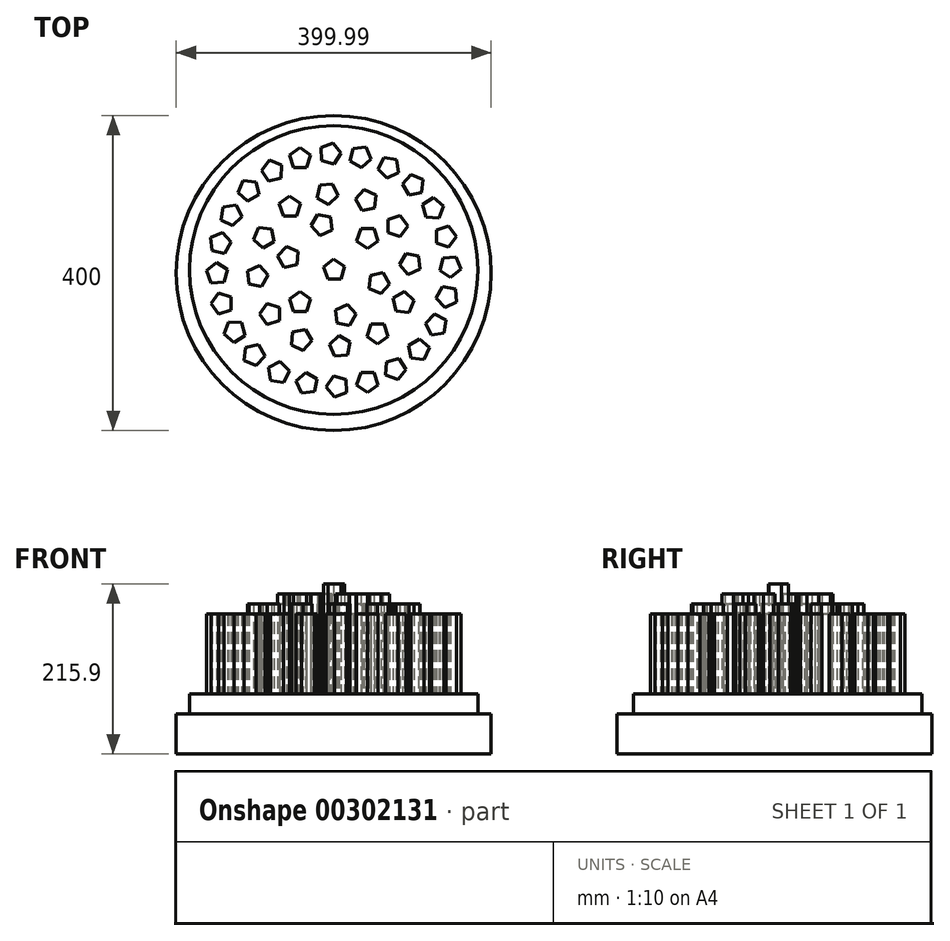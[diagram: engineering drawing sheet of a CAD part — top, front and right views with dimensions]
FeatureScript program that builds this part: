
annotation { "Feature Type Name" : "Feature", "Feature Type Description" : "" }
export const myFeature = defineFeature(function(context is Context, id is Id, definition is map)
    precondition{}
    {
        {
            var Q0;
            Q0=qCreatedBy(makeId("Top.planeOp"),FACE);
            var sketch = newSketch(context, id + "F0", { "sketchPlane" : qUnion([Q0])});
            skCircle(sketch, "E0.cCircle", {"center": v(0, 0) * mm, "radius": 11.36 * mm, "construction": true});
            skLineSegment(sketch, "E0.0", {"start": v(8.25, -11.36) * mm, "end": v(-8.25, -11.36) * mm});
            skLineSegment(sketch, "E0.1", {"start": v(-8.25, -11.36) * mm, "end": v(-13.35, 4.34) * mm});
            skLineSegment(sketch, "E0.2", {"start": v(-13.35, 4.34) * mm, "end": v(0, 14.04) * mm});
            skLineSegment(sketch, "E0.3", {"start": v(0, 14.04) * mm, "end": v(13.35, 4.34) * mm});
            skLineSegment(sketch, "E0.4", {"start": v(13.35, 4.34) * mm, "end": v(8.25, -11.36) * mm});
            skPoint(sketch, "E0.0.midPoint", {"position": v(0, -11.36) * mm});
            skLineSegment(sketch, "E1.1.0", {"start": v(46.76, -25.65) * mm, "end": v(45.03, -9.23) * mm});
            skLineSegment(sketch, "E1.1.1", {"start": v(45.03, -9.23) * mm, "end": v(60.11, -2.52) * mm});
            skLineSegment(sketch, "E1.1.2", {"start": v(60.11, -2.52) * mm, "end": v(71.16, -14.79) * mm});
            skLineSegment(sketch, "E1.1.3", {"start": v(71.16, -14.79) * mm, "end": v(62.9, -29.08) * mm});
            skLineSegment(sketch, "E1.1.4", {"start": v(62.9, -29.08) * mm, "end": v(46.76, -25.65) * mm});
            skLineSegment(sketch, "E1.2.0", {"start": v(102.78, 11.41) * mm, "end": v(87.7, 18.13) * mm});
            skLineSegment(sketch, "E1.2.1", {"start": v(87.7, 18.13) * mm, "end": v(89.43, 34.54) * mm});
            skLineSegment(sketch, "E1.2.2", {"start": v(89.43, 34.54) * mm, "end": v(105.57, 37.97) * mm});
            skLineSegment(sketch, "E1.2.3", {"start": v(105.57, 37.97) * mm, "end": v(113.83, 23.68) * mm});
            skLineSegment(sketch, "E1.2.4", {"start": v(113.83, 23.68) * mm, "end": v(102.78, 11.41) * mm});
            skLineSegment(sketch, "E1.3.0", {"start": v(98.7, 78.47) * mm, "end": v(85.34, 68.76) * mm});
            skLineSegment(sketch, "E1.3.1", {"start": v(85.34, 68.76) * mm, "end": v(72, 78.47) * mm});
            skLineSegment(sketch, "E1.3.2", {"start": v(72, 78.47) * mm, "end": v(77.1, 94.16) * mm});
            skLineSegment(sketch, "E1.3.3", {"start": v(77.1, 94.16) * mm, "end": v(93.6, 94.16) * mm});
            skLineSegment(sketch, "E1.3.4", {"start": v(93.6, 94.16) * mm, "end": v(98.7, 78.47) * mm});
            skLineSegment(sketch, "E1.4.2", {"start": v(25.23, 85.32) * mm, "end": v(14.19, 97.6) * mm});
            skLineSegment(sketch, "E1.5.0", {"start": v(42.73, 55.32) * mm, "end": v(56.41, 46.1) * mm});
            skLineSegment(sketch, "E1.5.1", {"start": v(56.41, 46.1) * mm, "end": v(51.86, 30.22) * mm});
            skLineSegment(sketch, "E1.5.2", {"start": v(51.86, 30.22) * mm, "end": v(35.37, 29.65) * mm});
            skLineSegment(sketch, "E1.5.3", {"start": v(35.37, 29.65) * mm, "end": v(29.72, 45.16) * mm});
            skLineSegment(sketch, "E1.5.4", {"start": v(29.72, 45.16) * mm, "end": v(42.73, 55.32) * mm});
            skPoint(sketch, "E1.center", {"position": v(42.67, 41.4) * mm});
            skLineSegment(sketch, "E2.1.0", {"start": v(-17.44, 71.39) * mm, "end": v(-2.36, 64.68) * mm});
            skLineSegment(sketch, "E2.1.1", {"start": v(-2.36, 64.68) * mm, "end": v(-4.08, 48.26) * mm});
            skLineSegment(sketch, "E2.1.2", {"start": v(-4.08, 48.26) * mm, "end": v(-20.23, 44.83) * mm});
            skLineSegment(sketch, "E2.1.3", {"start": v(-20.23, 44.83) * mm, "end": v(-28.48, 59.12) * mm});
            skLineSegment(sketch, "E2.1.4", {"start": v(-28.48, 59.12) * mm, "end": v(-17.44, 71.39) * mm});
            skLineSegment(sketch, "E2.2.0", {"start": v(38.59, 108.45) * mm, "end": v(40.31, 92.04) * mm});
            skLineSegment(sketch, "E2.2.1", {"start": v(40.31, 92.04) * mm, "end": v(25.23, 85.32) * mm});
            skLineSegment(sketch, "E2.2.3", {"start": v(14.19, 97.6) * mm, "end": v(22.44, 111.88) * mm});
            skLineSegment(sketch, "E2.2.4", {"start": v(22.44, 111.88) * mm, "end": v(38.59, 108.45) * mm});
            skLineSegment(sketch, "E2.anchor1", {"start": v(42.67, 41.4) * mm, "end": v(-8.25, -11.36) * mm, "construction": true});
            skLineSegment(sketch, "E3.0", {"start": v(-4.82, 110.21) * mm, "end": v(-21.32, 110.21) * mm});
            skLineSegment(sketch, "E3.1", {"start": v(-21.32, 110.21) * mm, "end": v(-26.42, 125.91) * mm});
            skLineSegment(sketch, "E3.2", {"start": v(-26.42, 125.91) * mm, "end": v(-13.07, 135.61) * mm});
            skLineSegment(sketch, "E3.3", {"start": v(-13.07, 135.61) * mm, "end": v(0.28, 125.91) * mm});
            skLineSegment(sketch, "E3.4", {"start": v(0.28, 125.91) * mm, "end": v(-4.82, 110.21) * mm});
            skPoint(sketch, "E3.0.midPoint", {"position": v(-13.07, 110.21) * mm});
            skLineSegment(sketch, "E4.1.0", {"start": v(41.5, 150.86) * mm, "end": v(48.22, 135.78) * mm});
            skLineSegment(sketch, "E4.1.1", {"start": v(25.09, 149.14) * mm, "end": v(41.5, 150.86) * mm});
            skLineSegment(sketch, "E4.1.2", {"start": v(21.66, 133) * mm, "end": v(25.09, 149.14) * mm});
            skLineSegment(sketch, "E4.1.3", {"start": v(35.95, 124.74) * mm, "end": v(21.66, 133) * mm});
            skLineSegment(sketch, "E4.1.4", {"start": v(48.22, 135.78) * mm, "end": v(35.95, 124.74) * mm});
            skLineSegment(sketch, "E4.2.0", {"start": v(96.4, 136.78) * mm, "end": v(94.66, 120.37) * mm});
            skLineSegment(sketch, "E4.2.1", {"start": v(81.31, 143.5) * mm, "end": v(96.4, 136.78) * mm});
            skLineSegment(sketch, "E4.2.2", {"start": v(70.27, 131.23) * mm, "end": v(81.31, 143.5) * mm});
            skLineSegment(sketch, "E4.2.3", {"start": v(78.52, 116.93) * mm, "end": v(70.27, 131.23) * mm});
            skLineSegment(sketch, "E4.2.4", {"start": v(94.66, 120.37) * mm, "end": v(78.52, 116.93) * mm});
            skLineSegment(sketch, "E4.3.0", {"start": v(136.88, 97.14) * mm, "end": v(127.18, 83.79) * mm});
            skLineSegment(sketch, "E4.3.1", {"start": v(127.18, 110.5) * mm, "end": v(136.88, 97.14) * mm});
            skLineSegment(sketch, "E4.3.2", {"start": v(111.48, 105.4) * mm, "end": v(127.18, 110.5) * mm});
            skLineSegment(sketch, "E4.3.3", {"start": v(111.48, 88.9) * mm, "end": v(111.48, 105.4) * mm});
            skLineSegment(sketch, "E4.3.4", {"start": v(127.18, 83.79) * mm, "end": v(111.48, 88.9) * mm});
            skLineSegment(sketch, "E4.4.0", {"start": v(152.13, 42.57) * mm, "end": v(137.05, 35.86) * mm});
            skLineSegment(sketch, "E4.4.1", {"start": v(150.4, 58.99) * mm, "end": v(152.13, 42.57) * mm});
            skLineSegment(sketch, "E4.4.2", {"start": v(134.26, 62.42) * mm, "end": v(150.4, 58.99) * mm});
            skLineSegment(sketch, "E4.4.3", {"start": v(126, 48.12) * mm, "end": v(134.26, 62.42) * mm});
            skLineSegment(sketch, "E4.4.4", {"start": v(137.05, 35.86) * mm, "end": v(126, 48.12) * mm});
            skLineSegment(sketch, "E4.5.0", {"start": v(138.05, -12.32) * mm, "end": v(121.64, -10.6) * mm});
            skLineSegment(sketch, "E4.5.1", {"start": v(144.76, 2.76) * mm, "end": v(138.05, -12.32) * mm});
            skLineSegment(sketch, "E4.5.2", {"start": v(132.5, 13.8) * mm, "end": v(144.76, 2.76) * mm});
            skLineSegment(sketch, "E4.5.3", {"start": v(118.2, 5.55) * mm, "end": v(132.5, 13.8) * mm});
            skLineSegment(sketch, "E4.5.4", {"start": v(121.64, -10.6) * mm, "end": v(118.2, 5.55) * mm});
            skLineSegment(sketch, "E4.6.0", {"start": v(98.41, -52.8) * mm, "end": v(85.06, -43.1) * mm});
            skLineSegment(sketch, "E4.6.1", {"start": v(111.77, -43.1) * mm, "end": v(98.41, -52.8) * mm});
            skLineSegment(sketch, "E4.6.2", {"start": v(106.67, -27.4) * mm, "end": v(111.77, -43.1) * mm});
            skLineSegment(sketch, "E4.6.3", {"start": v(90.16, -27.4) * mm, "end": v(106.67, -27.4) * mm});
            skLineSegment(sketch, "E4.6.4", {"start": v(85.06, -43.1) * mm, "end": v(90.16, -27.4) * mm});
            skLineSegment(sketch, "E4.7.0", {"start": v(43.84, -68.06) * mm, "end": v(37.13, -52.98) * mm});
            skLineSegment(sketch, "E4.7.1", {"start": v(60.26, -66.33) * mm, "end": v(43.84, -68.06) * mm});
            skLineSegment(sketch, "E4.7.2", {"start": v(63.69, -50.19) * mm, "end": v(60.26, -66.33) * mm});
            skLineSegment(sketch, "E4.7.3", {"start": v(49.4, -41.93) * mm, "end": v(63.69, -50.19) * mm});
            skLineSegment(sketch, "E4.7.4", {"start": v(37.13, -52.98) * mm, "end": v(49.4, -41.93) * mm});
            skLineSegment(sketch, "E4.8.0", {"start": v(-11.05, -53.98) * mm, "end": v(-9.32, -37.56) * mm});
            skLineSegment(sketch, "E4.8.1", {"start": v(4.03, -60.7) * mm, "end": v(-11.05, -53.98) * mm});
            skLineSegment(sketch, "E4.8.2", {"start": v(15.08, -48.42) * mm, "end": v(4.03, -60.7) * mm});
            skLineSegment(sketch, "E4.8.3", {"start": v(6.82, -34.13) * mm, "end": v(15.08, -48.42) * mm});
            skLineSegment(sketch, "E4.8.4", {"start": v(-9.32, -37.56) * mm, "end": v(6.82, -34.13) * mm});
            skLineSegment(sketch, "E4.9.0", {"start": v(-51.54, -14.34) * mm, "end": v(-41.84, -0.99) * mm});
            skLineSegment(sketch, "E4.9.1", {"start": v(-41.84, -27.7) * mm, "end": v(-51.54, -14.34) * mm});
            skLineSegment(sketch, "E4.9.2", {"start": v(-26.14, -22.6) * mm, "end": v(-41.84, -27.7) * mm});
            skLineSegment(sketch, "E4.9.3", {"start": v(-26.14, -6.09) * mm, "end": v(-26.14, -22.6) * mm});
            skLineSegment(sketch, "E4.9.4", {"start": v(-41.84, -0.99) * mm, "end": v(-26.14, -6.09) * mm});
            skLineSegment(sketch, "E4.10.0", {"start": v(-66.79, 40.23) * mm, "end": v(-51.7, 46.95) * mm});
            skLineSegment(sketch, "E4.10.1", {"start": v(-65.06, 23.82) * mm, "end": v(-66.79, 40.23) * mm});
            skLineSegment(sketch, "E4.10.2", {"start": v(-48.92, 20.39) * mm, "end": v(-65.06, 23.82) * mm});
            skLineSegment(sketch, "E4.10.3", {"start": v(-40.66, 34.68) * mm, "end": v(-48.92, 20.39) * mm});
            skLineSegment(sketch, "E4.10.4", {"start": v(-51.7, 46.95) * mm, "end": v(-40.66, 34.68) * mm});
            skLineSegment(sketch, "E4.11.0", {"start": v(-52.7, 95.12) * mm, "end": v(-36.3, 93.4) * mm});
            skLineSegment(sketch, "E4.11.1", {"start": v(-59.42, 80.04) * mm, "end": v(-52.7, 95.12) * mm});
            skLineSegment(sketch, "E4.11.2", {"start": v(-47.15, 69) * mm, "end": v(-59.42, 80.04) * mm});
            skLineSegment(sketch, "E4.11.3", {"start": v(-32.86, 77.25) * mm, "end": v(-47.15, 69) * mm});
            skLineSegment(sketch, "E4.11.4", {"start": v(-36.3, 93.4) * mm, "end": v(-32.86, 77.25) * mm});
            skLineSegment(sketch, "E5.0", {"start": v(8.25, 171.75) * mm, "end": v(-8.25, 171.75) * mm});
            skLineSegment(sketch, "E5.1", {"start": v(-8.25, 171.75) * mm, "end": v(-13.35, 187.44) * mm});
            skLineSegment(sketch, "E5.2", {"start": v(-13.35, 187.44) * mm, "end": v(0, 197.15) * mm});
            skLineSegment(sketch, "E5.3", {"start": v(0, 197.15) * mm, "end": v(13.35, 187.44) * mm});
            skLineSegment(sketch, "E5.4", {"start": v(13.35, 187.44) * mm, "end": v(8.25, 171.75) * mm});
            skLineSegment(sketch, "E6.1.0", {"start": v(-38.86, 180.8) * mm, "end": v(-23.45, 174.88) * mm});
            skLineSegment(sketch, "E6.1.1", {"start": v(-23.45, 174.88) * mm, "end": v(-24.3, 158.4) * mm});
            skLineSegment(sketch, "E6.1.2", {"start": v(-24.3, 158.4) * mm, "end": v(-40.25, 154.12) * mm});
            skLineSegment(sketch, "E6.1.3", {"start": v(-40.25, 154.12) * mm, "end": v(-49.24, 167.97) * mm});
            skLineSegment(sketch, "E6.1.4", {"start": v(-49.24, 167.97) * mm, "end": v(-38.86, 180.8) * mm});
            skLineSegment(sketch, "E6.2.0", {"start": v(-72.16, 154.94) * mm, "end": v(-55.74, 153.22) * mm});
            skLineSegment(sketch, "E6.2.1", {"start": v(-55.74, 153.22) * mm, "end": v(-52.3, 137.07) * mm});
            skLineSegment(sketch, "E6.2.2", {"start": v(-52.3, 137.07) * mm, "end": v(-66.6, 128.82) * mm});
            skLineSegment(sketch, "E6.2.3", {"start": v(-66.6, 128.82) * mm, "end": v(-78.87, 139.87) * mm});
            skLineSegment(sketch, "E6.2.4", {"start": v(-78.87, 139.87) * mm, "end": v(-72.16, 154.94) * mm});
            skLineSegment(sketch, "E6.3.0", {"start": v(-97.63, 121.36) * mm, "end": v(-81.33, 123.94) * mm});
            skLineSegment(sketch, "E6.3.1", {"start": v(-81.33, 123.94) * mm, "end": v(-73.83, 109.23) * mm});
            skLineSegment(sketch, "E6.3.2", {"start": v(-73.83, 109.23) * mm, "end": v(-85.5, 97.56) * mm});
            skLineSegment(sketch, "E6.3.3", {"start": v(-85.5, 97.56) * mm, "end": v(-100.21, 105.05) * mm});
            skLineSegment(sketch, "E6.3.4", {"start": v(-100.21, 105.05) * mm, "end": v(-97.63, 121.36) * mm});
            skLineSegment(sketch, "E6.4.0", {"start": v(-113.54, 82.32) * mm, "end": v(-98.46, 89.03) * mm});
            skLineSegment(sketch, "E6.4.1", {"start": v(-98.46, 89.03) * mm, "end": v(-87.42, 76.77) * mm});
            skLineSegment(sketch, "E6.4.2", {"start": v(-87.42, 76.77) * mm, "end": v(-95.67, 62.47) * mm});
            skLineSegment(sketch, "E6.4.3", {"start": v(-95.67, 62.47) * mm, "end": v(-111.82, 65.9) * mm});
            skLineSegment(sketch, "E6.4.4", {"start": v(-111.82, 65.9) * mm, "end": v(-113.54, 82.32) * mm});
            skLineSegment(sketch, "E6.5.0", {"start": v(-118.8, 40.5) * mm, "end": v(-105.98, 50.88) * mm});
            skLineSegment(sketch, "E6.5.1", {"start": v(-105.98, 50.88) * mm, "end": v(-92.14, 41.9) * mm});
            skLineSegment(sketch, "E6.5.2", {"start": v(-92.14, 41.9) * mm, "end": v(-96.41, 25.95) * mm});
            skLineSegment(sketch, "E6.5.3", {"start": v(-96.41, 25.95) * mm, "end": v(-112.9, 25.08) * mm});
            skLineSegment(sketch, "E6.5.4", {"start": v(-112.9, 25.08) * mm, "end": v(-118.8, 40.5) * mm});
            skLineSegment(sketch, "E6.6.0", {"start": v(-113.07, -1.27) * mm, "end": v(-103.37, 12.08) * mm});
            skLineSegment(sketch, "E6.6.1", {"start": v(-103.37, 12.08) * mm, "end": v(-87.67, 6.98) * mm});
            skLineSegment(sketch, "E6.6.2", {"start": v(-87.67, 6.98) * mm, "end": v(-87.67, -9.52) * mm});
            skLineSegment(sketch, "E6.6.3", {"start": v(-87.67, -9.52) * mm, "end": v(-103.37, -14.62) * mm});
            skLineSegment(sketch, "E6.6.4", {"start": v(-103.37, -14.62) * mm, "end": v(-113.07, -1.27) * mm});
            skLineSegment(sketch, "E6.7.0", {"start": v(-96.72, -40.13) * mm, "end": v(-90.8, -24.72) * mm});
            skLineSegment(sketch, "E6.7.1", {"start": v(-90.8, -24.72) * mm, "end": v(-74.32, -25.58) * mm});
            skLineSegment(sketch, "E6.7.2", {"start": v(-74.32, -25.58) * mm, "end": v(-70.05, -41.52) * mm});
            skLineSegment(sketch, "E6.7.3", {"start": v(-70.05, -41.52) * mm, "end": v(-83.9, -50.51) * mm});
            skLineSegment(sketch, "E6.7.4", {"start": v(-83.9, -50.51) * mm, "end": v(-96.72, -40.13) * mm});
            skLineSegment(sketch, "E6.8.0", {"start": v(-70.87, -73.43) * mm, "end": v(-69.15, -57) * mm});
            skLineSegment(sketch, "E6.8.1", {"start": v(-69.15, -57) * mm, "end": v(-53, -53.58) * mm});
            skLineSegment(sketch, "E6.8.2", {"start": v(-53, -53.58) * mm, "end": v(-44.75, -67.87) * mm});
            skLineSegment(sketch, "E6.8.3", {"start": v(-44.75, -67.87) * mm, "end": v(-55.8, -80.14) * mm});
            skLineSegment(sketch, "E6.8.4", {"start": v(-55.8, -80.14) * mm, "end": v(-70.87, -73.43) * mm});
            skLineSegment(sketch, "E6.9.0", {"start": v(-37.28, -98.9) * mm, "end": v(-39.86, -82.6) * mm});
            skLineSegment(sketch, "E6.9.1", {"start": v(-39.86, -82.6) * mm, "end": v(-25.16, -75.1) * mm});
            skLineSegment(sketch, "E6.9.2", {"start": v(-25.16, -75.1) * mm, "end": v(-13.49, -86.77) * mm});
            skLineSegment(sketch, "E6.9.3", {"start": v(-13.49, -86.77) * mm, "end": v(-20.98, -101.48) * mm});
            skLineSegment(sketch, "E6.9.4", {"start": v(-20.98, -101.48) * mm, "end": v(-37.28, -98.9) * mm});
            skLineSegment(sketch, "E6.10.0", {"start": v(1.75, -114.81) * mm, "end": v(-4.96, -99.73) * mm});
            skLineSegment(sketch, "E6.10.1", {"start": v(-4.96, -99.73) * mm, "end": v(7.3, -88.69) * mm});
            skLineSegment(sketch, "E6.10.2", {"start": v(7.3, -88.69) * mm, "end": v(21.6, -96.94) * mm});
            skLineSegment(sketch, "E6.10.3", {"start": v(21.6, -96.94) * mm, "end": v(18.17, -113.09) * mm});
            skLineSegment(sketch, "E6.10.4", {"start": v(18.17, -113.09) * mm, "end": v(1.75, -114.81) * mm});
            skLineSegment(sketch, "E6.11.0", {"start": v(43.58, -120.08) * mm, "end": v(33.2, -107.25) * mm});
            skLineSegment(sketch, "E6.11.1", {"start": v(33.2, -107.25) * mm, "end": v(42.18, -93.4) * mm});
            skLineSegment(sketch, "E6.11.2", {"start": v(42.18, -93.4) * mm, "end": v(58.13, -97.68) * mm});
            skLineSegment(sketch, "E6.11.3", {"start": v(58.13, -97.68) * mm, "end": v(58.99, -114.16) * mm});
            skLineSegment(sketch, "E6.11.4", {"start": v(58.99, -114.16) * mm, "end": v(43.58, -120.08) * mm});
            skLineSegment(sketch, "E6.12.0", {"start": v(85.34, -114.34) * mm, "end": v(72, -104.64) * mm});
            skLineSegment(sketch, "E6.12.1", {"start": v(72, -104.64) * mm, "end": v(77.1, -88.94) * mm});
            skLineSegment(sketch, "E6.12.2", {"start": v(77.1, -88.94) * mm, "end": v(93.6, -88.94) * mm});
            skLineSegment(sketch, "E6.12.3", {"start": v(93.6, -88.94) * mm, "end": v(98.7, -104.64) * mm});
            skLineSegment(sketch, "E6.12.4", {"start": v(98.7, -104.64) * mm, "end": v(85.34, -114.34) * mm});
            skLineSegment(sketch, "E6.13.0", {"start": v(124.2, -98) * mm, "end": v(108.8, -92.08) * mm});
            skLineSegment(sketch, "E6.13.1", {"start": v(108.8, -92.08) * mm, "end": v(109.65, -75.6) * mm});
            skLineSegment(sketch, "E6.13.2", {"start": v(109.65, -75.6) * mm, "end": v(125.6, -71.32) * mm});
            skLineSegment(sketch, "E6.13.3", {"start": v(125.6, -71.32) * mm, "end": v(134.59, -85.16) * mm});
            skLineSegment(sketch, "E6.13.4", {"start": v(134.59, -85.16) * mm, "end": v(124.2, -98) * mm});
            skLineSegment(sketch, "E6.14.0", {"start": v(157.5, -72.14) * mm, "end": v(141.08, -70.42) * mm});
            skLineSegment(sketch, "E6.14.1", {"start": v(141.08, -70.42) * mm, "end": v(137.65, -54.27) * mm});
            skLineSegment(sketch, "E6.14.2", {"start": v(137.65, -54.27) * mm, "end": v(151.95, -46.02) * mm});
            skLineSegment(sketch, "E6.14.3", {"start": v(151.95, -46.02) * mm, "end": v(164.21, -57.06) * mm});
            skLineSegment(sketch, "E6.14.4", {"start": v(164.21, -57.06) * mm, "end": v(157.5, -72.14) * mm});
            skLineSegment(sketch, "E6.15.0", {"start": v(182.97, -38.55) * mm, "end": v(166.67, -41.13) * mm});
            skLineSegment(sketch, "E6.15.1", {"start": v(166.67, -41.13) * mm, "end": v(159.18, -26.43) * mm});
            skLineSegment(sketch, "E6.15.2", {"start": v(159.18, -26.43) * mm, "end": v(170.85, -14.76) * mm});
            skLineSegment(sketch, "E6.15.3", {"start": v(170.85, -14.76) * mm, "end": v(185.56, -22.25) * mm});
            skLineSegment(sketch, "E6.15.4", {"start": v(185.56, -22.25) * mm, "end": v(182.97, -38.55) * mm});
            skLineSegment(sketch, "E6.16.0", {"start": v(198.89, 0.48) * mm, "end": v(183.8, -6.23) * mm});
            skLineSegment(sketch, "E6.16.1", {"start": v(183.8, -6.23) * mm, "end": v(172.76, 6.04) * mm});
            skLineSegment(sketch, "E6.16.2", {"start": v(172.76, 6.04) * mm, "end": v(181.02, 20.33) * mm});
            skLineSegment(sketch, "E6.16.3", {"start": v(181.02, 20.33) * mm, "end": v(197.16, 16.9) * mm});
            skLineSegment(sketch, "E6.16.4", {"start": v(197.16, 16.9) * mm, "end": v(198.89, 0.48) * mm});
            skLineSegment(sketch, "E6.17.0", {"start": v(204.15, 42.31) * mm, "end": v(191.33, 31.92) * mm});
            skLineSegment(sketch, "E6.17.1", {"start": v(191.33, 31.92) * mm, "end": v(177.48, 40.91) * mm});
            skLineSegment(sketch, "E6.17.2", {"start": v(177.48, 40.91) * mm, "end": v(181.76, 56.86) * mm});
            skLineSegment(sketch, "E6.17.3", {"start": v(181.76, 56.86) * mm, "end": v(198.24, 57.72) * mm});
            skLineSegment(sketch, "E6.17.4", {"start": v(198.24, 57.72) * mm, "end": v(204.15, 42.31) * mm});
            skLineSegment(sketch, "E6.18.0", {"start": v(198.42, 84.07) * mm, "end": v(188.71, 70.72) * mm});
            skLineSegment(sketch, "E6.18.1", {"start": v(188.71, 70.72) * mm, "end": v(173.02, 75.82) * mm});
            skLineSegment(sketch, "E6.18.2", {"start": v(173.02, 75.82) * mm, "end": v(173.02, 92.33) * mm});
            skLineSegment(sketch, "E6.18.3", {"start": v(173.02, 92.33) * mm, "end": v(188.71, 97.43) * mm});
            skLineSegment(sketch, "E6.18.4", {"start": v(188.71, 97.43) * mm, "end": v(198.42, 84.07) * mm});
            skLineSegment(sketch, "E6.19.0", {"start": v(182.07, 122.93) * mm, "end": v(176.15, 107.52) * mm});
            skLineSegment(sketch, "E6.19.1", {"start": v(176.15, 107.52) * mm, "end": v(159.67, 108.38) * mm});
            skLineSegment(sketch, "E6.19.2", {"start": v(159.67, 108.38) * mm, "end": v(155.4, 124.33) * mm});
            skLineSegment(sketch, "E6.19.3", {"start": v(155.4, 124.33) * mm, "end": v(169.24, 133.32) * mm});
            skLineSegment(sketch, "E6.19.4", {"start": v(169.24, 133.32) * mm, "end": v(182.07, 122.93) * mm});
            skLineSegment(sketch, "E6.20.0", {"start": v(156.21, 156.23) * mm, "end": v(154.49, 139.81) * mm});
            skLineSegment(sketch, "E6.20.1", {"start": v(154.49, 139.81) * mm, "end": v(138.34, 136.38) * mm});
            skLineSegment(sketch, "E6.20.2", {"start": v(138.34, 136.38) * mm, "end": v(130.1, 150.68) * mm});
            skLineSegment(sketch, "E6.20.3", {"start": v(130.1, 150.68) * mm, "end": v(141.14, 162.94) * mm});
            skLineSegment(sketch, "E6.20.4", {"start": v(141.14, 162.94) * mm, "end": v(156.21, 156.23) * mm});
            skLineSegment(sketch, "E6.21.0", {"start": v(122.63, 181.7) * mm, "end": v(125.2, 165.4) * mm});
            skLineSegment(sketch, "E6.21.1", {"start": v(125.2, 165.4) * mm, "end": v(110.5, 157.9) * mm});
            skLineSegment(sketch, "E6.21.2", {"start": v(110.5, 157.9) * mm, "end": v(98.83, 169.58) * mm});
            skLineSegment(sketch, "E6.21.3", {"start": v(98.83, 169.58) * mm, "end": v(106.32, 184.29) * mm});
            skLineSegment(sketch, "E6.21.4", {"start": v(106.32, 184.29) * mm, "end": v(122.63, 181.7) * mm});
            skLineSegment(sketch, "E6.22.0", {"start": v(83.59, 197.62) * mm, "end": v(90.3, 182.54) * mm});
            skLineSegment(sketch, "E6.22.1", {"start": v(90.3, 182.54) * mm, "end": v(78.04, 171.5) * mm});
            skLineSegment(sketch, "E6.22.2", {"start": v(78.04, 171.5) * mm, "end": v(63.74, 179.75) * mm});
            skLineSegment(sketch, "E6.22.3", {"start": v(63.74, 179.75) * mm, "end": v(67.17, 195.9) * mm});
            skLineSegment(sketch, "E6.22.4", {"start": v(67.17, 195.9) * mm, "end": v(83.59, 197.62) * mm});
            skLineSegment(sketch, "E6.23.0", {"start": v(41.76, 202.88) * mm, "end": v(52.15, 190.06) * mm});
            skLineSegment(sketch, "E6.23.1", {"start": v(52.15, 190.06) * mm, "end": v(43.16, 176.21) * mm});
            skLineSegment(sketch, "E6.23.2", {"start": v(43.16, 176.21) * mm, "end": v(27.22, 180.49) * mm});
            skLineSegment(sketch, "E6.23.3", {"start": v(27.22, 180.49) * mm, "end": v(26.35, 196.97) * mm});
            skLineSegment(sketch, "E6.23.4", {"start": v(26.35, 196.97) * mm, "end": v(41.76, 202.88) * mm});
            skCircle(sketch, "E7", {"center": v(42.67, 41.4) * mm, "radius": 183.27 * mm});
            skCircle(sketch, "E8", {"center": v(42.67, 37.54) * mm, "radius": 200 * mm});
            skPoint(sketch, "E9.secondSnap0", {"position": v(104.67, 163.74) * mm});
            skSolve(sketch);
        }
        {
            var Q0;
            Q0 = qSketchRegion(id + "F0", true);
            var Q1;
            Q1=makeQuery(id+"F0.imprint","IMPRINT",FACE,{"disambiguationData":[TD([[makeQuery(id+"F0.imprint","IMPRINT",EDGE,{"derivedFrom":sQuery(id+"F0.wireOp",EDGE,"E4.1.0")}),-1.0]])]});
            var Q2;
            Q2=makeQuery(id+"F0.imprint","IMPRINT",FACE,{"disambiguationData":[TD([[makeQuery(id+"F0.imprint","IMPRINT",EDGE,{"derivedFrom":sQuery(id+"F0.wireOp",EDGE,"E4.2.0")}),-1.0]])]});
            var Q3;
            Q3=makeQuery(id+"F0.imprint","IMPRINT",FACE,{"disambiguationData":[TD([[makeQuery(id+"F0.imprint","IMPRINT",EDGE,{"derivedFrom":sQuery(id+"F0.wireOp",EDGE,"E1.4.2")}),-1.0]])]});
            var Q4;
            Q4=makeQuery(id+"F0.imprint","IMPRINT",FACE,{"disambiguationData":[TD([[makeQuery(id+"F0.imprint","IMPRINT",EDGE,{"derivedFrom":sQuery(id+"F0.wireOp",EDGE,"E3.0")}),-1.0]])]});
            var Q5;
            Q5=makeQuery(id+"F0.imprint","IMPRINT",FACE,{"disambiguationData":[TD([[makeQuery(id+"F0.imprint","IMPRINT",EDGE,{"derivedFrom":sQuery(id+"F0.wireOp",EDGE,"E4.11.0")}),-1.0]])]});
            var Q6;
            Q6=makeQuery(id+"F0.imprint","IMPRINT",FACE,{"disambiguationData":[TD([[makeQuery(id+"F0.imprint","IMPRINT",EDGE,{"derivedFrom":sQuery(id+"F0.wireOp",EDGE,"E4.10.0")}),-1.0]])]});
            var Q7;
            Q7=makeQuery(id+"F0.imprint","IMPRINT",FACE,{"disambiguationData":[TD([[makeQuery(id+"F0.imprint","IMPRINT",EDGE,{"derivedFrom":sQuery(id+"F0.wireOp",EDGE,"E2.1.0")}),-1.0]])]});
            var Q8;
            Q8=makeQuery(id+"F0.imprint","IMPRINT",FACE,{"disambiguationData":[TD([[makeQuery(id+"F0.imprint","IMPRINT",EDGE,{"derivedFrom":sQuery(id+"F0.wireOp",EDGE,"E1.5.0")}),-1.0]])]});
            var Q9;
            Q9=makeQuery(id+"F0.imprint","IMPRINT",FACE,{"disambiguationData":[TD([[makeQuery(id+"F0.imprint","IMPRINT",EDGE,{"derivedFrom":sQuery(id+"F0.wireOp",EDGE,"E0.0")}),-1.0]])]});
            var Q10;
            Q10=makeQuery(id+"F0.imprint","IMPRINT",FACE,{"disambiguationData":[TD([[makeQuery(id+"F0.imprint","IMPRINT",EDGE,{"derivedFrom":sQuery(id+"F0.wireOp",EDGE,"E4.8.0")}),-1.0]])]});
            var Q11;
            Q11=makeQuery(id+"F0.imprint","IMPRINT",FACE,{"disambiguationData":[TD([[makeQuery(id+"F0.imprint","IMPRINT",EDGE,{"derivedFrom":sQuery(id+"F0.wireOp",EDGE,"E4.7.0")}),-1.0]])]});
            var Q12;
            Q12=makeQuery(id+"F0.imprint","IMPRINT",FACE,{"disambiguationData":[TD([[makeQuery(id+"F0.imprint","IMPRINT",EDGE,{"derivedFrom":sQuery(id+"F0.wireOp",EDGE,"E1.1.0")}),-1.0]])]});
            var Q13;
            Q13=makeQuery(id+"F0.imprint","IMPRINT",FACE,{"disambiguationData":[TD([[makeQuery(id+"F0.imprint","IMPRINT",EDGE,{"derivedFrom":sQuery(id+"F0.wireOp",EDGE,"E4.6.0")}),-1.0]])]});
            var Q14;
            Q14=makeQuery(id+"F0.imprint","IMPRINT",FACE,{"disambiguationData":[TD([[makeQuery(id+"F0.imprint","IMPRINT",EDGE,{"derivedFrom":sQuery(id+"F0.wireOp",EDGE,"E1.2.0")}),-1.0]])]});
            var Q15;
            Q15=makeQuery(id+"F0.imprint","IMPRINT",FACE,{"disambiguationData":[TD([[makeQuery(id+"F0.imprint","IMPRINT",EDGE,{"derivedFrom":sQuery(id+"F0.wireOp",EDGE,"E0.0")}),1.0]])]});
            var Q16;
            Q16=makeQuery(id+"F0.imprint","IMPRINT",FACE,{"disambiguationData":[TD([[makeQuery(id+"F0.imprint","IMPRINT",EDGE,{"derivedFrom":sQuery(id+"F0.wireOp",EDGE,"E4.4.0")}),-1.0]])]});
            var Q17;
            Q17=makeQuery(id+"F0.imprint","IMPRINT",FACE,{"disambiguationData":[TD([[makeQuery(id+"F0.imprint","IMPRINT",EDGE,{"derivedFrom":sQuery(id+"F0.wireOp",EDGE,"E1.3.0")}),-1.0]])]});
            var Q18;
            Q18=makeQuery(id+"F0.imprint","IMPRINT",FACE,{"disambiguationData":[TD([[makeQuery(id+"F0.imprint","IMPRINT",EDGE,{"derivedFrom":sQuery(id+"F0.wireOp",EDGE,"E4.3.0")}),-1.0]])]});
            var Q19;
            Q19=makeQuery(id+"F0.imprint","IMPRINT",FACE,{"disambiguationData":[TD([[makeQuery(id+"F0.imprint","IMPRINT",EDGE,{"derivedFrom":sQuery(id+"F0.wireOp",EDGE,"E6.21.0")}),-1.0]])]});
            var Q20;
            Q20=makeQuery(id+"F0.imprint","IMPRINT",FACE,{"disambiguationData":[TD([[makeQuery(id+"F0.imprint","IMPRINT",EDGE,{"derivedFrom":sQuery(id+"F0.wireOp",EDGE,"E6.23.0")}),-1.0]])]});
            var Q21;
            Q21=makeQuery(id+"F0.imprint","IMPRINT",FACE,{"disambiguationData":[TD([[makeQuery(id+"F0.imprint","IMPRINT",EDGE,{"derivedFrom":sQuery(id+"F0.wireOp",EDGE,"E6.22.0")}),-1.0]])]});
            var Q22;
            Q22=makeQuery(id+"F0.imprint","IMPRINT",FACE,{"disambiguationData":[TD([[makeQuery(id+"F0.imprint","IMPRINT",EDGE,{"derivedFrom":sQuery(id+"F0.wireOp",EDGE,"E5.0")}),-1.0]])]});
            var Q23;
            Q23=makeQuery(id+"F0.imprint","IMPRINT",FACE,{"disambiguationData":[TD([[makeQuery(id+"F0.imprint","IMPRINT",EDGE,{"derivedFrom":sQuery(id+"F0.wireOp",EDGE,"E6.1.0")}),-1.0]])]});
            var Q24;
            Q24=makeQuery(id+"F0.imprint","IMPRINT",FACE,{"disambiguationData":[TD([[makeQuery(id+"F0.imprint","IMPRINT",EDGE,{"derivedFrom":sQuery(id+"F0.wireOp",EDGE,"E6.2.0")}),-1.0]])]});
            var Q25;
            Q25=makeQuery(id+"F0.imprint","IMPRINT",FACE,{"disambiguationData":[TD([[makeQuery(id+"F0.imprint","IMPRINT",EDGE,{"derivedFrom":sQuery(id+"F0.wireOp",EDGE,"E6.3.0")}),-1.0]])]});
            var Q26;
            Q26=makeQuery(id+"F0.imprint","IMPRINT",FACE,{"disambiguationData":[TD([[makeQuery(id+"F0.imprint","IMPRINT",EDGE,{"derivedFrom":sQuery(id+"F0.wireOp",EDGE,"E6.4.0")}),-1.0]])]});
            var Q27;
            Q27=makeQuery(id+"F0.imprint","IMPRINT",FACE,{"disambiguationData":[TD([[makeQuery(id+"F0.imprint","IMPRINT",EDGE,{"derivedFrom":sQuery(id+"F0.wireOp",EDGE,"E6.5.0")}),-1.0]])]});
            var Q28;
            Q28=makeQuery(id+"F0.imprint","IMPRINT",FACE,{"disambiguationData":[TD([[makeQuery(id+"F0.imprint","IMPRINT",EDGE,{"derivedFrom":sQuery(id+"F0.wireOp",EDGE,"E6.6.0")}),-1.0]])]});
            var Q29;
            Q29=makeQuery(id+"F0.imprint","IMPRINT",FACE,{"disambiguationData":[TD([[makeQuery(id+"F0.imprint","IMPRINT",EDGE,{"derivedFrom":sQuery(id+"F0.wireOp",EDGE,"E4.9.0")}),-1.0]])]});
            var Q30;
            Q30=makeQuery(id+"F0.imprint","IMPRINT",FACE,{"disambiguationData":[TD([[makeQuery(id+"F0.imprint","IMPRINT",EDGE,{"derivedFrom":sQuery(id+"F0.wireOp",EDGE,"E6.7.0")}),-1.0]])]});
            var Q31;
            Q31=makeQuery(id+"F0.imprint","IMPRINT",FACE,{"disambiguationData":[TD([[makeQuery(id+"F0.imprint","IMPRINT",EDGE,{"derivedFrom":sQuery(id+"F0.wireOp",EDGE,"E6.8.0")}),-1.0]])]});
            var Q32;
            Q32=makeQuery(id+"F0.imprint","IMPRINT",FACE,{"disambiguationData":[TD([[makeQuery(id+"F0.imprint","IMPRINT",EDGE,{"derivedFrom":sQuery(id+"F0.wireOp",EDGE,"E6.9.0")}),-1.0]])]});
            var Q33;
            Q33=makeQuery(id+"F0.imprint","IMPRINT",FACE,{"disambiguationData":[TD([[makeQuery(id+"F0.imprint","IMPRINT",EDGE,{"derivedFrom":sQuery(id+"F0.wireOp",EDGE,"E6.10.0")}),-1.0]])]});
            var Q34;
            Q34=makeQuery(id+"F0.imprint","IMPRINT",FACE,{"disambiguationData":[TD([[makeQuery(id+"F0.imprint","IMPRINT",EDGE,{"derivedFrom":sQuery(id+"F0.wireOp",EDGE,"E6.11.0")}),-1.0]])]});
            var Q35;
            Q35=makeQuery(id+"F0.imprint","IMPRINT",FACE,{"disambiguationData":[TD([[makeQuery(id+"F0.imprint","IMPRINT",EDGE,{"derivedFrom":sQuery(id+"F0.wireOp",EDGE,"E6.12.0")}),-1.0]])]});
            var Q36;
            Q36=makeQuery(id+"F0.imprint","IMPRINT",FACE,{"disambiguationData":[TD([[makeQuery(id+"F0.imprint","IMPRINT",EDGE,{"derivedFrom":sQuery(id+"F0.wireOp",EDGE,"E6.13.0")}),-1.0]])]});
            var Q37;
            Q37=makeQuery(id+"F0.imprint","IMPRINT",FACE,{"disambiguationData":[TD([[makeQuery(id+"F0.imprint","IMPRINT",EDGE,{"derivedFrom":sQuery(id+"F0.wireOp",EDGE,"E6.14.0")}),-1.0]])]});
            var Q38;
            Q38=makeQuery(id+"F0.imprint","IMPRINT",FACE,{"disambiguationData":[TD([[makeQuery(id+"F0.imprint","IMPRINT",EDGE,{"derivedFrom":sQuery(id+"F0.wireOp",EDGE,"E6.15.0")}),-1.0]])]});
            var Q39;
            Q39=makeQuery(id+"F0.imprint","IMPRINT",FACE,{"disambiguationData":[TD([[makeQuery(id+"F0.imprint","IMPRINT",EDGE,{"derivedFrom":sQuery(id+"F0.wireOp",EDGE,"E6.16.0")}),-1.0]])]});
            var Q40;
            Q40=makeQuery(id+"F0.imprint","IMPRINT",FACE,{"disambiguationData":[TD([[makeQuery(id+"F0.imprint","IMPRINT",EDGE,{"derivedFrom":sQuery(id+"F0.wireOp",EDGE,"E4.5.0")}),-1.0]])]});
            var Q41;
            Q41=makeQuery(id+"F0.imprint","IMPRINT",FACE,{"disambiguationData":[TD([[makeQuery(id+"F0.imprint","IMPRINT",EDGE,{"derivedFrom":sQuery(id+"F0.wireOp",EDGE,"E6.17.0")}),-1.0]])]});
            var Q42;
            Q42=makeQuery(id+"F0.imprint","IMPRINT",FACE,{"disambiguationData":[TD([[makeQuery(id+"F0.imprint","IMPRINT",EDGE,{"derivedFrom":sQuery(id+"F0.wireOp",EDGE,"E6.18.0")}),-1.0]])]});
            var Q43;
            Q43=makeQuery(id+"F0.imprint","IMPRINT",FACE,{"disambiguationData":[TD([[makeQuery(id+"F0.imprint","IMPRINT",EDGE,{"derivedFrom":sQuery(id+"F0.wireOp",EDGE,"E6.19.0")}),-1.0]])]});
            var Q44;
            Q44=makeQuery(id+"F0.imprint","IMPRINT",FACE,{"disambiguationData":[TD([[makeQuery(id+"F0.imprint","IMPRINT",EDGE,{"derivedFrom":sQuery(id+"F0.wireOp",EDGE,"E6.20.0")}),-1.0]])]});
            extrude(context, id + "F1", {"entities" : qUnion([Q0, Q1, Q2, Q3, Q4, Q5, Q6, Q7, Q8, Q9, Q10, Q11, Q12, Q13, Q14, Q15, Q16, Q17, Q18, Q19, Q20, Q21, Q22, Q23, Q24, Q25, Q26, Q27, Q28, Q29, Q30, Q31, Q32, Q33, Q34, Q35, Q36, Q37, Q38, Q39, Q40, Q41, Q42, Q43, Q44]), "oppositeDirection" : true, "depth" : 76.2 * mm});
        }
        {
            var Q0;
            Q0=makeQuery(id+"F0.imprint","IMPRINT",FACE,{"disambiguationData":[TD([[makeQuery(id+"F0.imprint","IMPRINT",EDGE,{"derivedFrom":sQuery(id+"F0.wireOp",EDGE,"E7")}),-1.0]])]});
            extrude(context, id + "F2", {"entities" : qUnion([Q0]), "operationType" : NewBodyOperationType.REMOVE, "oppositeDirection" : true, "depth" : 25.4 * mm});
        }
        {
            var Q0;
            Q0=makeQuery(id+"F0.imprint","IMPRINT",FACE,{"disambiguationData":[TD([[makeQuery(id+"F0.imprint","IMPRINT",EDGE,{"derivedFrom":sQuery(id+"F0.wireOp",EDGE,"E6.3.0")}),-1.0]])]});
            var Q1;
            Q1=makeQuery(id+"F0.imprint","IMPRINT",FACE,{"disambiguationData":[TD([[makeQuery(id+"F0.imprint","IMPRINT",EDGE,{"derivedFrom":sQuery(id+"F0.wireOp",EDGE,"E6.2.0")}),-1.0]])]});
            var Q2;
            Q2=makeQuery(id+"F0.imprint","IMPRINT",FACE,{"disambiguationData":[TD([[makeQuery(id+"F0.imprint","IMPRINT",EDGE,{"derivedFrom":sQuery(id+"F0.wireOp",EDGE,"E6.1.0")}),-1.0]])]});
            var Q3;
            Q3=makeQuery(id+"F0.imprint","IMPRINT",FACE,{"disambiguationData":[TD([[makeQuery(id+"F0.imprint","IMPRINT",EDGE,{"derivedFrom":sQuery(id+"F0.wireOp",EDGE,"E5.0")}),-1.0]])]});
            var Q4;
            Q4=makeQuery(id+"F0.imprint","IMPRINT",FACE,{"disambiguationData":[TD([[makeQuery(id+"F0.imprint","IMPRINT",EDGE,{"derivedFrom":sQuery(id+"F0.wireOp",EDGE,"E6.23.0")}),-1.0]])]});
            var Q5;
            Q5=makeQuery(id+"F0.imprint","IMPRINT",FACE,{"disambiguationData":[TD([[makeQuery(id+"F0.imprint","IMPRINT",EDGE,{"derivedFrom":sQuery(id+"F0.wireOp",EDGE,"E6.22.0")}),-1.0]])]});
            var Q6;
            Q6=makeQuery(id+"F0.imprint","IMPRINT",FACE,{"disambiguationData":[TD([[makeQuery(id+"F0.imprint","IMPRINT",EDGE,{"derivedFrom":sQuery(id+"F0.wireOp",EDGE,"E6.21.0")}),-1.0]])]});
            var Q7;
            Q7=makeQuery(id+"F0.imprint","IMPRINT",FACE,{"disambiguationData":[TD([[makeQuery(id+"F0.imprint","IMPRINT",EDGE,{"derivedFrom":sQuery(id+"F0.wireOp",EDGE,"E6.20.0")}),-1.0]])]});
            var Q8;
            Q8=makeQuery(id+"F0.imprint","IMPRINT",FACE,{"disambiguationData":[TD([[makeQuery(id+"F0.imprint","IMPRINT",EDGE,{"derivedFrom":sQuery(id+"F0.wireOp",EDGE,"E6.19.0")}),-1.0]])]});
            var Q9;
            Q9=makeQuery(id+"F0.imprint","IMPRINT",FACE,{"disambiguationData":[TD([[makeQuery(id+"F0.imprint","IMPRINT",EDGE,{"derivedFrom":sQuery(id+"F0.wireOp",EDGE,"E6.18.0")}),-1.0]])]});
            var Q10;
            Q10=makeQuery(id+"F0.imprint","IMPRINT",FACE,{"disambiguationData":[TD([[makeQuery(id+"F0.imprint","IMPRINT",EDGE,{"derivedFrom":sQuery(id+"F0.wireOp",EDGE,"E6.17.0")}),-1.0]])]});
            var Q11;
            Q11=makeQuery(id+"F0.imprint","IMPRINT",FACE,{"disambiguationData":[TD([[makeQuery(id+"F0.imprint","IMPRINT",EDGE,{"derivedFrom":sQuery(id+"F0.wireOp",EDGE,"E6.16.0")}),-1.0]])]});
            var Q12;
            Q12=makeQuery(id+"F0.imprint","IMPRINT",FACE,{"disambiguationData":[TD([[makeQuery(id+"F0.imprint","IMPRINT",EDGE,{"derivedFrom":sQuery(id+"F0.wireOp",EDGE,"E6.15.0")}),-1.0]])]});
            var Q13;
            Q13=makeQuery(id+"F0.imprint","IMPRINT",FACE,{"disambiguationData":[TD([[makeQuery(id+"F0.imprint","IMPRINT",EDGE,{"derivedFrom":sQuery(id+"F0.wireOp",EDGE,"E6.14.0")}),-1.0]])]});
            var Q14;
            Q14=makeQuery(id+"F0.imprint","IMPRINT",FACE,{"disambiguationData":[TD([[makeQuery(id+"F0.imprint","IMPRINT",EDGE,{"derivedFrom":sQuery(id+"F0.wireOp",EDGE,"E6.13.0")}),-1.0]])]});
            var Q15;
            Q15=makeQuery(id+"F0.imprint","IMPRINT",FACE,{"disambiguationData":[TD([[makeQuery(id+"F0.imprint","IMPRINT",EDGE,{"derivedFrom":sQuery(id+"F0.wireOp",EDGE,"E6.12.0")}),-1.0]])]});
            var Q16;
            Q16=makeQuery(id+"F0.imprint","IMPRINT",FACE,{"disambiguationData":[TD([[makeQuery(id+"F0.imprint","IMPRINT",EDGE,{"derivedFrom":sQuery(id+"F0.wireOp",EDGE,"E6.11.0")}),-1.0]])]});
            var Q17;
            Q17=makeQuery(id+"F0.imprint","IMPRINT",FACE,{"disambiguationData":[TD([[makeQuery(id+"F0.imprint","IMPRINT",EDGE,{"derivedFrom":sQuery(id+"F0.wireOp",EDGE,"E6.10.0")}),-1.0]])]});
            var Q18;
            Q18=makeQuery(id+"F0.imprint","IMPRINT",FACE,{"disambiguationData":[TD([[makeQuery(id+"F0.imprint","IMPRINT",EDGE,{"derivedFrom":sQuery(id+"F0.wireOp",EDGE,"E6.9.0")}),-1.0]])]});
            var Q19;
            Q19=makeQuery(id+"F0.imprint","IMPRINT",FACE,{"disambiguationData":[TD([[makeQuery(id+"F0.imprint","IMPRINT",EDGE,{"derivedFrom":sQuery(id+"F0.wireOp",EDGE,"E6.8.0")}),-1.0]])]});
            var Q20;
            Q20=makeQuery(id+"F0.imprint","IMPRINT",FACE,{"disambiguationData":[TD([[makeQuery(id+"F0.imprint","IMPRINT",EDGE,{"derivedFrom":sQuery(id+"F0.wireOp",EDGE,"E6.7.0")}),-1.0]])]});
            var Q21;
            Q21=makeQuery(id+"F0.imprint","IMPRINT",FACE,{"disambiguationData":[TD([[makeQuery(id+"F0.imprint","IMPRINT",EDGE,{"derivedFrom":sQuery(id+"F0.wireOp",EDGE,"E6.6.0")}),-1.0]])]});
            var Q22;
            Q22=makeQuery(id+"F0.imprint","IMPRINT",FACE,{"disambiguationData":[TD([[makeQuery(id+"F0.imprint","IMPRINT",EDGE,{"derivedFrom":sQuery(id+"F0.wireOp",EDGE,"E6.5.0")}),-1.0]])]});
            var Q23;
            Q23=makeQuery(id+"F0.imprint","IMPRINT",FACE,{"disambiguationData":[TD([[makeQuery(id+"F0.imprint","IMPRINT",EDGE,{"derivedFrom":sQuery(id+"F0.wireOp",EDGE,"E6.4.0")}),-1.0]])]});
            extrude(context, id + "F3", {"entities" : qUnion([Q0, Q1, Q2, Q3, Q4, Q5, Q6, Q7, Q8, Q9, Q10, Q11, Q12, Q13, Q14, Q15, Q16, Q17, Q18, Q19, Q20, Q21, Q22, Q23]), "operationType" : NewBodyOperationType.ADD, "depth" : 101.6 * mm});
        }
        {
            var Q0;
            Q0=makeQuery(id+"F0.imprint","IMPRINT",FACE,{"disambiguationData":[TD([[makeQuery(id+"F0.imprint","IMPRINT",EDGE,{"derivedFrom":sQuery(id+"F0.wireOp",EDGE,"E4.6.0")}),-1.0]])]});
            var Q1;
            Q1=makeQuery(id+"F0.imprint","IMPRINT",FACE,{"disambiguationData":[TD([[makeQuery(id+"F0.imprint","IMPRINT",EDGE,{"derivedFrom":sQuery(id+"F0.wireOp",EDGE,"E4.7.0")}),-1.0]])]});
            var Q2;
            Q2=makeQuery(id+"F0.imprint","IMPRINT",FACE,{"disambiguationData":[TD([[makeQuery(id+"F0.imprint","IMPRINT",EDGE,{"derivedFrom":sQuery(id+"F0.wireOp",EDGE,"E4.8.0")}),-1.0]])]});
            var Q3;
            Q3=makeQuery(id+"F0.imprint","IMPRINT",FACE,{"disambiguationData":[TD([[makeQuery(id+"F0.imprint","IMPRINT",EDGE,{"derivedFrom":sQuery(id+"F0.wireOp",EDGE,"E4.9.0")}),-1.0]])]});
            var Q4;
            Q4=makeQuery(id+"F0.imprint","IMPRINT",FACE,{"disambiguationData":[TD([[makeQuery(id+"F0.imprint","IMPRINT",EDGE,{"derivedFrom":sQuery(id+"F0.wireOp",EDGE,"E4.10.0")}),-1.0]])]});
            var Q5;
            Q5=makeQuery(id+"F0.imprint","IMPRINT",FACE,{"disambiguationData":[TD([[makeQuery(id+"F0.imprint","IMPRINT",EDGE,{"derivedFrom":sQuery(id+"F0.wireOp",EDGE,"E4.11.0")}),-1.0]])]});
            var Q6;
            Q6=makeQuery(id+"F0.imprint","IMPRINT",FACE,{"disambiguationData":[TD([[makeQuery(id+"F0.imprint","IMPRINT",EDGE,{"derivedFrom":sQuery(id+"F0.wireOp",EDGE,"E3.0")}),-1.0]])]});
            var Q7;
            Q7=makeQuery(id+"F0.imprint","IMPRINT",FACE,{"disambiguationData":[TD([[makeQuery(id+"F0.imprint","IMPRINT",EDGE,{"derivedFrom":sQuery(id+"F0.wireOp",EDGE,"E4.1.0")}),-1.0]])]});
            var Q8;
            Q8=makeQuery(id+"F0.imprint","IMPRINT",FACE,{"disambiguationData":[TD([[makeQuery(id+"F0.imprint","IMPRINT",EDGE,{"derivedFrom":sQuery(id+"F0.wireOp",EDGE,"E4.2.0")}),-1.0]])]});
            var Q9;
            Q9=makeQuery(id+"F0.imprint","IMPRINT",FACE,{"disambiguationData":[TD([[makeQuery(id+"F0.imprint","IMPRINT",EDGE,{"derivedFrom":sQuery(id+"F0.wireOp",EDGE,"E4.3.0")}),-1.0]])]});
            var Q10;
            Q10=makeQuery(id+"F0.imprint","IMPRINT",FACE,{"disambiguationData":[TD([[makeQuery(id+"F0.imprint","IMPRINT",EDGE,{"derivedFrom":sQuery(id+"F0.wireOp",EDGE,"E4.4.0")}),-1.0]])]});
            var Q11;
            Q11=makeQuery(id+"F0.imprint","IMPRINT",FACE,{"disambiguationData":[TD([[makeQuery(id+"F0.imprint","IMPRINT",EDGE,{"derivedFrom":sQuery(id+"F0.wireOp",EDGE,"E4.5.0")}),-1.0]])]});
            extrude(context, id + "F4", {"entities" : qUnion([Q0, Q1, Q2, Q3, Q4, Q5, Q6, Q7, Q8, Q9, Q10, Q11]), "operationType" : NewBodyOperationType.ADD, "depth" : 114.3 * mm});
        }
        {
            var Q0;
            Q0=makeQuery(id+"F0.imprint","IMPRINT",FACE,{"disambiguationData":[TD([[makeQuery(id+"F0.imprint","IMPRINT",EDGE,{"derivedFrom":sQuery(id+"F0.wireOp",EDGE,"E2.1.0")}),-1.0]])]});
            var Q1;
            Q1=makeQuery(id+"F0.imprint","IMPRINT",FACE,{"disambiguationData":[TD([[makeQuery(id+"F0.imprint","IMPRINT",EDGE,{"derivedFrom":sQuery(id+"F0.wireOp",EDGE,"E1.4.2")}),-1.0]])]});
            var Q2;
            Q2=makeQuery(id+"F0.imprint","IMPRINT",FACE,{"disambiguationData":[TD([[makeQuery(id+"F0.imprint","IMPRINT",EDGE,{"derivedFrom":sQuery(id+"F0.wireOp",EDGE,"E1.3.0")}),-1.0]])]});
            var Q3;
            Q3=makeQuery(id+"F0.imprint","IMPRINT",FACE,{"disambiguationData":[TD([[makeQuery(id+"F0.imprint","IMPRINT",EDGE,{"derivedFrom":sQuery(id+"F0.wireOp",EDGE,"E1.2.0")}),-1.0]])]});
            var Q4;
            Q4=makeQuery(id+"F0.imprint","IMPRINT",FACE,{"disambiguationData":[TD([[makeQuery(id+"F0.imprint","IMPRINT",EDGE,{"derivedFrom":sQuery(id+"F0.wireOp",EDGE,"E1.1.0")}),-1.0]])]});
            var Q5;
            Q5=makeQuery(id+"F0.imprint","IMPRINT",FACE,{"disambiguationData":[TD([[makeQuery(id+"F0.imprint","IMPRINT",EDGE,{"derivedFrom":sQuery(id+"F0.wireOp",EDGE,"E0.0")}),-1.0]])]});
            extrude(context, id + "F5", {"entities" : qUnion([Q0, Q1, Q2, Q3, Q4, Q5]), "operationType" : NewBodyOperationType.ADD, "depth" : 127 * mm});
        }
        {
            var Q0;
            Q0=makeQuery(id+"F0.imprint","IMPRINT",FACE,{"disambiguationData":[TD([[makeQuery(id+"F0.imprint","IMPRINT",EDGE,{"derivedFrom":sQuery(id+"F0.wireOp",EDGE,"E1.5.0")}),-1.0]])]});
            extrude(context, id + "F6", {"entities" : qUnion([Q0]), "operationType" : NewBodyOperationType.ADD, "depth" : 139.7 * mm});
        }
    });
